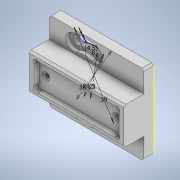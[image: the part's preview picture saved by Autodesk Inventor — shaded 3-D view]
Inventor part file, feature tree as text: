
AUTODESK INVENTOR PART (.ipt)
format: ipt  version: 2020 (Build 240168000, 168)  size: 346,624 bytes
history: native  units: in
note: dims shown in document units (in); Inventor stores cm internally (conversion verified against a paired STEP export)
features: sketch x13, extrude x10, hole x6, chamfer x3
ambient origin geometry x8: Origin, YZ Plane, XZ Plane, XY Plane, X Axis, Y Axis, Z Axis, Center Point
bodies: Solid1 (feature_tree)
feature tree (32):
  extrude  "Extrusion1"  TaperAngle=0.0deg  [1 undecoded]
  hole  "Hole1"  [1 undecoded]
  hole  "Hole2"  [1 undecoded]
  sketch  "Sketch4"  dims[d14=0.7165in]
  hole  "Hole3"  [1 undecoded]
  extrude  "Extrusion2"  Depth=0.0394in
  extrude  "Extrusion3"  TaperAngle=0.0deg  [1 undecoded]
  hole  "Hole5"  [1 undecoded]
  chamfer  "Chamfer2"  Distance=0.0827in
  sketch  "Sketch8"  dims[d25=0.0in d26=0.0in]
  hole  "Hole6"  [1 undecoded]
  extrude  "Extrusion4"  TaperAngle=0.0deg  [1 undecoded]
  extrude  "Extrusion5"  TaperAngle=0.0deg  [1 undecoded]
  extrude  "Extrusion6"  TaperAngle=0.0deg  [1 undecoded]
  chamfer  "Chamfer5"  Distance=0.0787in Angle=45.0deg
  chamfer  "Chamfer6"  Distance=0.0394in
  sketch  "Sketch12"  dims[d30=0.0827in d31=0.224in d32=0.315in d33=0.1654in d34=0.5635in d35=0.0827in d36=0.0in d37=0.0827in d38=0.0in]
  extrude  "Extrusion12"  Depth=0.0413in
  extrude  "Extrusion13"  Depth=0.3937in
  hole  "Hole7"  [1 undecoded]
  sketch  "Sketch15"  dims[d41=0.1969in d42=0.0in d54=0.0in]
  sketch  "Sketch17"  dims[d55=0.0in d56=0.0in d57=0.0in d58=0.1575in d59=0.224in d60=0.315in d61=0.0787in d62=0.5635in d63=0.0197in d64=0.0in d68=0.0394in d69=0.0787in d70=45.0deg d77=0.0394in d78=0.0413in d79=0.3937in d80=0.0in d81=0.0in d82=0.1969in d83=0.0827in d84=0.224in d85=0.315in d86=0.0787in d87=0.5635in d88=0.0827in d89=0.0in d90=0.0827in d91=0.0in d92=1.0in d93=0.0in d94=0.4862in d95=0.0in d96=0.0in d97=1.9213in d98=0.748in d99=1.7244in d100=0.5512in d101=0.0984in d102=0.0in d103=0.0394in d104=0.0787in d105=45.0deg d106=0.1181in d107=45.0deg d108=45.0deg d109=45.0deg d110=0.1181in d111=0.1181in d112=0.1181in d113=0.0394in d114=0.0787in d115=45.0deg d118=0.315in d122=0.1772in d129=0.0in d130=0.0in d131=0.0787in d132=0.0in d133=0.0827in d134=0.2362in d135=0.1575in d136=0.0787in d137=90.0deg d138=0.0827in d139=0.0in d140=1.5354in d141=0.9055in d142=1.3976in d143=1.0433in d147=0.315in d148=0.1772in d149=0.1772in d150=0.315in d151=0.0in d152=0.0in d153=0.0787in d154=0.0in d127=0.0197in d128=0.0344in]
  extrude  "Extrusion14"  TaperAngle=0.0deg  [1 undecoded]
  extrude  "Extrusion15"  Depth=0.1969in
  sketch  "Sketch1"  dims[d2=0.5059in d3=0.0in]
  sketch  "Sketch2"  dims[d4=0.0849in d5=0.224in d6=0.1575in d7=0.0787in d8=90.0deg d9=0.3492in d10=0.0in d11=0.0in]
  sketch  "Sketch3"  dims[d12=0.0in d13=1.4331in]
  sketch  "Sketch5"  dims[d15=0.1772in d16=0.224in d17=0.315in d18=0.3445in d19=0.5635in d20=0.3492in d21=0.0in d22=0.0in]
  sketch  "Sketch7"  dims[d23=0.0in d24=0.0394in]
  sketch  "Sketch9"  dims[d27=0.3937in d28=0.1969in]
  sketch  "Sketch10"  dims[d29=0.0413in]
  sketch  "Sketch14"  dims[d39=1.9213in d40=1.6142in]
note: 12 required parameter values undecoded (feature->parameter linkage not recoverable at this tier; creation-order binding heuristic only, values carry confidence <= 0.55)
